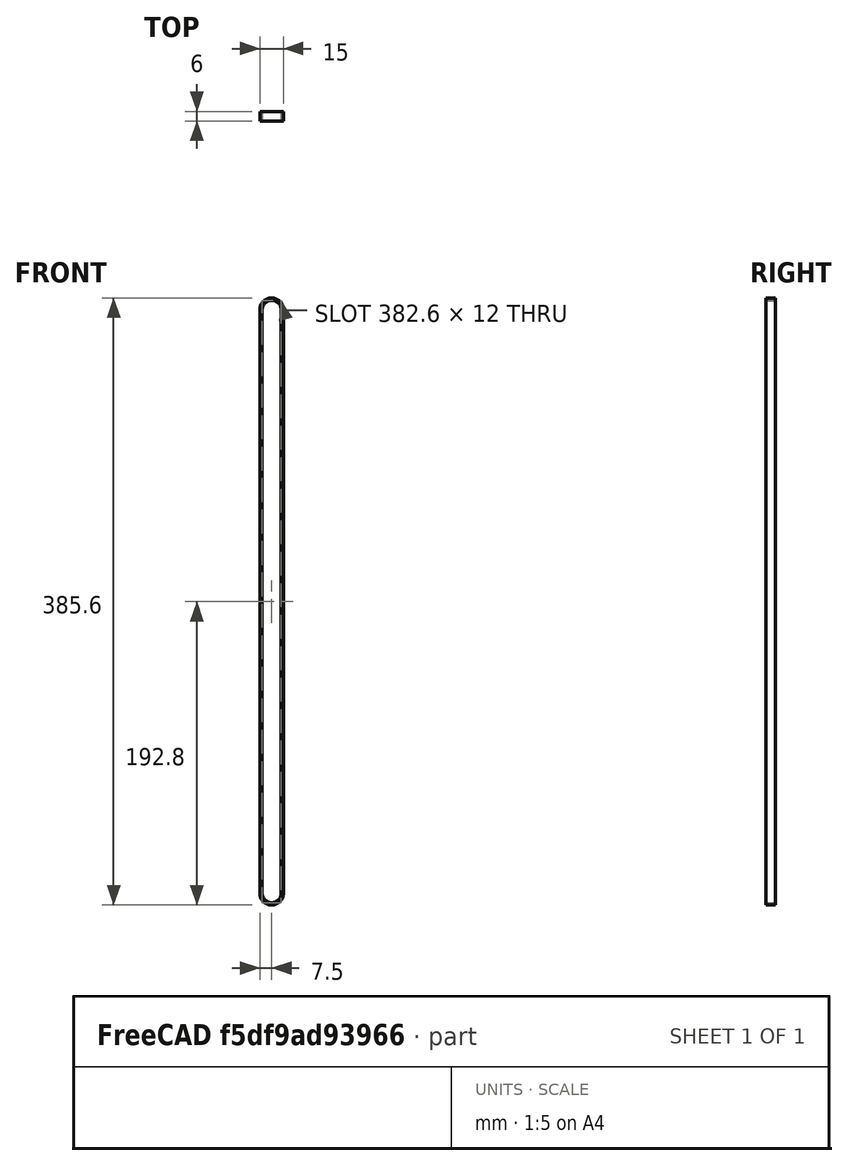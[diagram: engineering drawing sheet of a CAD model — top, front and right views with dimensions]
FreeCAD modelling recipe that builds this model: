
FCSTD DOCUMENT  (FreeCAD 0.18R)
Label: drive-belt
License: All rights reserved
LicenseURL: http://en.wikipedia.org/wiki/All_rights_reserved
objects: Sketcher::SketchObject×1, PartDesign::Pad×1, PartDesign::Body×1
note: 4 computed .brp shape members not serialized (recipe doc carries the construction recipe); baked Part::Feature solids carry a one-line shape summary decoded from their .brp

FEATURE [Sketcher::SketchObject] Sketch
  MapMode = 5
  Placement = pos=(0,0,0) rot=(1,0,0;1.5708rad)
  Support = -> [XZ_Plane]
  sketch-geometry (8):
    g0: ArcOfCircle CenterX=4.5e-15 CenterY=0 CenterZ=0 NormalX=0 NormalY=0 NormalZ=1 AngleXU=0 Radius=6 StartAngle=3.14159 EndAngle=6.28319
    g1: ArcOfCircle CenterX=0 CenterY=370.6 CenterZ=0 NormalX=0 NormalY=0 NormalZ=1 AngleXU=0 Radius=6 StartAngle=6.28319 EndAngle=9.42478
    g2: ArcOfCircle CenterX=0 CenterY=370.6 CenterZ=0 NormalX=0 NormalY=0 NormalZ=1 AngleXU=0 Radius=7.5 StartAngle=2.7e-15 EndAngle=3.14159
    g3: ArcOfCircle CenterX=4.5e-15 CenterY=0 CenterZ=0 NormalX=0 NormalY=0 NormalZ=1 AngleXU=0 Radius=7.5 StartAngle=3.14159 EndAngle=6.28319
    g4: LineSegment StartX=-7.5 StartY=370.6 StartZ=0 EndX=-7.5 EndY=6.6883e-08 EndZ=0
    g5: LineSegment StartX=7.5 StartY=1.79653e-07 StartZ=0 EndX=7.5 EndY=370.6 EndZ=0
    g6: LineSegment StartX=-6 StartY=7e-16 StartZ=0 EndX=-6 EndY=370.6 EndZ=0
    g7: LineSegment StartX=6 StartY=370.6 StartZ=0 EndX=6 EndY=0 EndZ=0
  constraints (26):
    c: Diameter(g0) = 12
    c: Equal(g1,g0)
    c: Diameter(g2) = 15
    c: Coincident(g2,g1)
    c: Diameter(g3) = 15
    c: Coincident(g3,g0)
    c: Vertical(g4)
    c: Tangent(g4,g3)
    c: Vertical(g5)
    c: Tangent(g5,g3)
    c: Coincident(g2,g5)
    c: Coincident(g2,g4)
    c: Coincident(g3,g4)
    c: Coincident(g3,g5)
    c: Vertical(g6)
    c: Vertical(g7)
    c: Coincident(g0,g6)
    c: Coincident(g0,g7)
    c: Coincident(g1,g7)
    c: Coincident(g1,g6)
    c: DistanceY(g0,g1) = 370.6
    c: PointOnObject(g1,g-2)
    c: PointOnObject(g0,g-1)
    c: PointOnObject(g0,g-1)
    c: PointOnObject(g0,g-1)
    c: DistanceY(g2,g1) = 0
FEATURE [PartDesign::Pad] Pad
  Length = 6
  Length2 = 100
  Placement = pos=(0,0,0) rot=(1,0,0;1.5708rad)
  Profile = -> Sketch
  Type = 0
FEATURE [PartDesign::Body] Body  label="y-drive-belt"
  Group = -> [Sketch,Pad]
  Origin = -> Origin
  Placement = pos=(185,-184.75,-87) rot=(0,0,1;0rad)
  Tip = -> Pad
